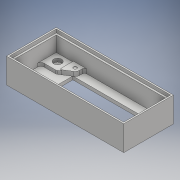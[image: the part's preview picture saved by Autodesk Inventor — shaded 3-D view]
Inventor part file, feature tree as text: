
AUTODESK INVENTOR PART (.ipt)
format: ipt  version: 2018 (Build 220112000, 112)  size: 358,400 bytes
history: native  units: mm
features: extrude x13, projected_geometry x13, sketch x11, hole x1
ambient origin geometry x8: Origin, YZ Plane, XZ Plane, XY Plane, X Axis, Y Axis, Z Axis, Center Point
bodies: Solid1 (feature_tree)
feature tree (38):
  extrude  "bottom"  Depth=3.0mm
  extrude  "walls"  Depth=3.1mm
  hole  "holes"  [1 undecoded]
  extrude  "display"  Depth=39.0mm
  extrude  "Extrusion19"  Depth=3.5mm
  extrude  "bolt holes"  Depth=8.0mm
  extrude  "holes screws"  Depth=6.2mm
  extrude  "fill after hole"  Depth=3.0mm
  extrude  "collar"  Depth=3.0mm
  extrude  "encoder standoff"  TaperAngle=0.0deg  [1 undecoded]
  extrude  "encoder hole"  Depth=1.3mm
  extrude  "encoder nut"  TaperAngle=0.0deg  [1 undecoded]
  extrude  "encoder fill before hole"  Depth=3.0mm TaperAngle=0.0deg
  extrude  "Extrusion21"  Depth=15.5mm
  sketch  "Sketch1"  dims[d2=3.0mm d3=0.0mm d30=3.0mm]
  sketch  "Sketch5"  dims[d31=19.6mm d32=0.0mm d33=3.1mm]
  projected_geometry  "Projected Loop6"
  projected_geometry  "Projected Loop7"
  sketch  "Sketch8"  dims[d34=75.0mm d35=31.0mm]
  sketch  "Sketch10"  dims[d45=100.0mm d46=39.0mm]
  sketch  "Sketch11"  dims[d50=3.5mm d51=3.5mm]
  projected_geometry  "Projected Loop8"
  projected_geometry  "Projected Loop9"
  projected_geometry  "Projected Loop10"
  projected_geometry  "Projected Loop11"
  sketch  "Sketch12"  dims[d52=0.0mm d53=0.0mm d54=8.0mm]
  projected_geometry  "Projected Loop12"
  projected_geometry  "Projected Loop14"
  sketch  "Sketch13"  dims[d57=6.2mm d58=6.2mm]
  projected_geometry  "Projected Loop15"
  sketch  "Sketch14"  dims[d59=6.5mm d60=0.0mm d61=3.0mm]
  sketch  "Sketch15"  dims[d62=3.0mm d65=3.0mm]
  sketch  "Sketch16"  dims[d66=3.0mm d67=0.0mm d68=0.0mm]
  sketch  "Sketch18"  dims[d69=0.6mm d70=0.0mm d71=7.2mm d73=0.0mm d74=0.0mm d79=3.0mm d80=0.0mm d81=15.5mm d82=13.0mm d83=1.0mm d87=14.0mm d88=2.5mm d89=0.0mm d90=14.0mm d91=3.0mm d92=0.0mm d93=0.6mm d94=0.0mm d95=3.0mm d96=2.0mm d99=1.5mm d100=1.5mm d101=3.5mm d102=2.8mm d103=1.5mm d104=1.5mm d105=2.0mm d106=2.0mm d109=6.2mm d112=6.5mm d113=3.8mm d114=0.0mm d117=2.0mm d118=5.0mm d119=5.0mm d120=2.0mm d121=2.0mm d122=2.0mm d123=5.0mm d124=0.1mm d125=0.0mm d126=1.3mm d127=1.3mm d128=1.3mm d129=1.3mm]
  projected_geometry  "Projected Loop21"
  projected_geometry  "Projected Loop22"
  projected_geometry  "Projected Loop23"
  projected_geometry  "Projected Loop24"
note: 3 required parameter values undecoded (feature->parameter linkage not recoverable at this tier; creation-order binding heuristic only, values carry confidence <= 0.55)
